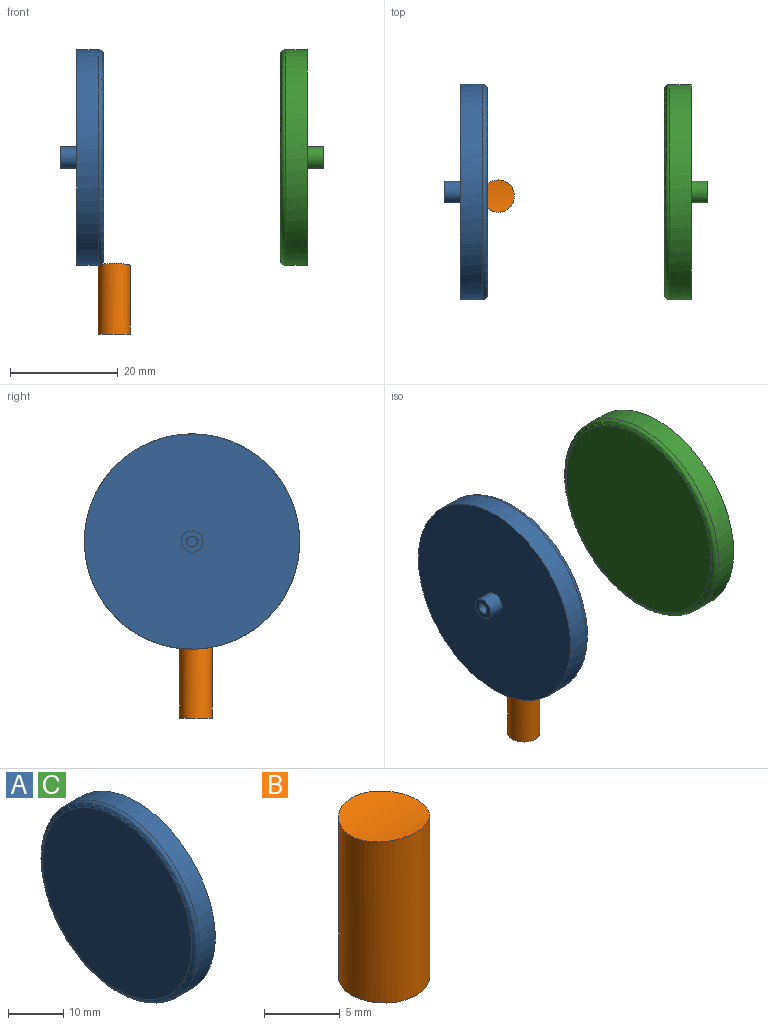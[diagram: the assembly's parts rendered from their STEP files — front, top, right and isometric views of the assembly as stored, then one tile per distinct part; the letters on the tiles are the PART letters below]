
ASSEMBLY  parts=3 mates=2
PART A: 8 faces, bbox 8x43.3x43.3 mm
  f0: cylinder r=20mm len=40mm, axis (-1,0,0), area 502.7mm2, adj f1,f3
  f1: plane 40x40mm, normal (1,0,0), area 1244.1mm2, adj f0,f5
  f2: plane 38x38mm, normal (-1,0,0), area 1134.1mm2, adj f3
  f3: torus R=19mm, axis (1,0,0), area 193.8mm2, adj f0,f2
  f4: cylinder r=1mm len=3mm, axis (-1,0,0), area 18.8mm2, adj f6,f7
  f5: cylinder r=2mm len=4mm, axis (-1,0,0), area 37.7mm2, adj f1,f6
  f6: plane 4x4mm, normal (1,0,0), area 9.4mm2, adj f4,f5
  f7: plane 2x2mm, normal (1,0,0), area 3.1mm2, adj f4
PART B: 5 faces, bbox 6x6x13.2 mm
  f0: cylinder r=20mm len=6mm, axis (1,0,0), area 28.4mm2, adj f4
  f1: cylinder r=21.49mm len=4mm, axis (1,0,0), area 12.6mm2, adj f2
  f2: cylinder r=2mm len=11.49mm, axis (0,0,-1), area 142.9mm2, adj f1,f3
  f3: plane 6x6mm, normal (0,0,-1), area 15.7mm2, adj f2,f4
  f4: cylinder r=3mm len=13.15mm, axis (0,0,-1), area 243.7mm2, adj f0,f3
PART C: same geometry as A
PLACE A rot(axis=(0,-0.74,0.68),180deg) t=(-66.07,165.48,39.88)mm
PLACE B t=(-54.11,221.42,39.88)mm fixed
PLACE C rot(axis=(-1,0,0),25deg) t=(-33.24,165.48,39.88)mm
MATE cylindrical A.f0 <-> B.f0  axis (-1,0,0) through (-71.07,165.48,39.88)mm
MATE cylindrical C.f0 <-> B.f0  axis (-1,0,0) through (-30.24,165.48,39.88)mm
